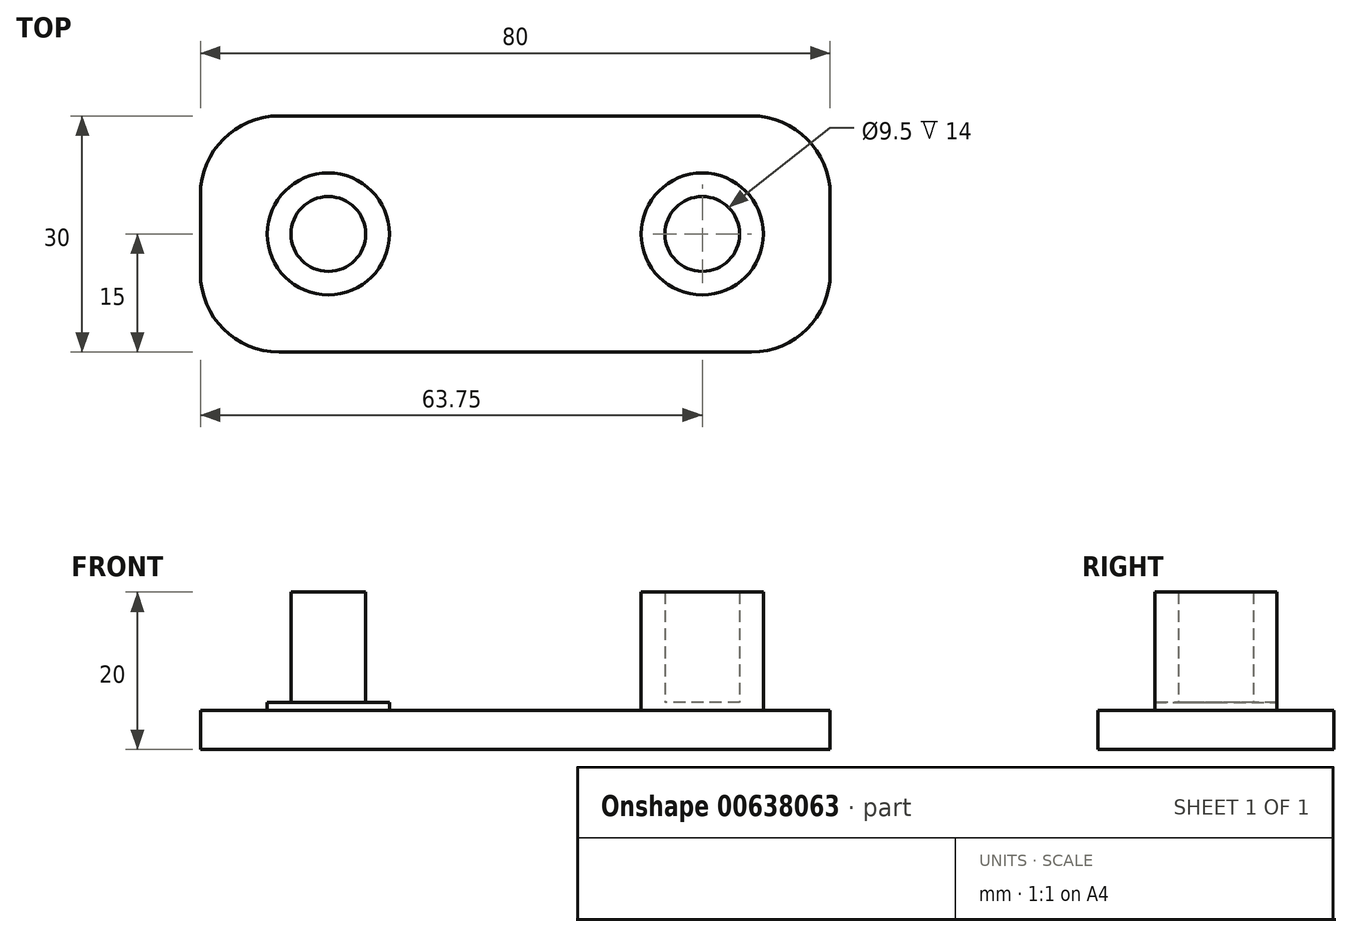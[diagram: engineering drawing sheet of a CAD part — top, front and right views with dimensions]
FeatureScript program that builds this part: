
annotation { "Feature Type Name" : "Feature", "Feature Type Description" : "" }
export const myFeature = defineFeature(function(context is Context, id is Id, definition is map)
    precondition{}
    {
        {
            var Q0;
            Q0=qCreatedBy(makeId("Top.planeOp"),FACE);
            var sketch = newSketch(context, id + "F0", { "sketchPlane" : qUnion([Q0])});
            skLineSegment(sketch, "E0.bottom", {"start": v(10, 0) * mm, "end": v(70, 0) * mm});
            skLineSegment(sketch, "E0.top", {"start": v(10, -30) * mm, "end": v(70, -30) * mm});
            skLineSegment(sketch, "E0.left", {"start": v(0, -10) * mm, "end": v(0, -20) * mm});
            skLineSegment(sketch, "E0.right", {"start": v(80, -10) * mm, "end": v(80, -20) * mm});
            skCircle(sketch, "E1", {"center": v(16.25, -15) * mm, "radius": 4.75 * mm});
            skLineSegment(sketch, "E2", {"start": v(0, -15) * mm, "end": v(80, -15) * mm, "construction": true});
            skLineSegment(sketch, "E3", {"start": v(40, 0) * mm, "end": v(40, -30) * mm, "construction": true});
            skCircle(sketch, "E4.MirrorC", {"center": v(63.75, -15) * mm, "radius": 4.75 * mm});
            skCircle(sketch, "E5", {"center": v(16.25, -15) * mm, "radius": 7.75 * mm});
            skCircle(sketch, "E6.MirrorC", {"center": v(63.75, -15) * mm, "radius": 7.75 * mm});
            skPoint(sketch, "E7.visualSharp", {"position": v(0, 0) * mm});
            skArc(sketch, "E7.filletArc", {"start": v(10, 0) * mm, "mid": v(2.93, -2.93) * mm, "end": v(0, -10) * mm});
            skPoint(sketch, "E8.visualSharp", {"position": v(80, 0) * mm});
            skArc(sketch, "E8.filletArc", {"start": v(80, -10) * mm, "mid": v(77.07, -2.93) * mm, "end": v(70, 0) * mm});
            skPoint(sketch, "E9.visualSharp", {"position": v(80, -30) * mm});
            skArc(sketch, "E9.filletArc", {"start": v(70, -30) * mm, "mid": v(77.07, -27.07) * mm, "end": v(80, -20) * mm});
            skPoint(sketch, "E10.visualSharp", {"position": v(0, -30) * mm});
            skArc(sketch, "E10.filletArc", {"start": v(0, -20) * mm, "mid": v(2.93, -27.07) * mm, "end": v(10, -30) * mm});
            skSolve(sketch);
        }
        {
            var Q0;
            Q0 = qSketchRegion(id + "F0", true);
            extrude(context, id + "F1", {"entities" : qUnion([Q0]), "depth" : 5 * mm, "offsetDistance" : 25 * mm});
        }
        {
            var Q0;
            Q0=makeQuery(id+"F0.imprint","IMPRINT",FACE,{"disambiguationData":[TD([[makeQuery(id+"F0.imprint","IMPRINT",EDGE,{"derivedFrom":sQuery(id+"F0.wireOp",EDGE,"E1")}),-1.0]])]});
            var Q1;
            Q1=makeQuery(id+"F0.imprint","IMPRINT",FACE,{"disambiguationData":[TD([[makeQuery(id+"F0.imprint","IMPRINT",EDGE,{"derivedFrom":sQuery(id+"F0.wireOp",EDGE,"E4.MirrorC")}),1.0]])]});
            extrude(context, id + "F2", {"entities" : qUnion([Q0, Q1]), "operationType" : NewBodyOperationType.ADD, "depth" : 6 * mm, "offsetDistance" : 25 * mm});
        }
        {
            var Q0;
            Q0=makeQuery(id+"F0.imprint","IMPRINT",FACE,{"disambiguationData":[TD([[makeQuery(id+"F0.imprint","IMPRINT",EDGE,{"derivedFrom":sQuery(id+"F0.wireOp",EDGE,"E1")}),1.0]])]});
            var Q1;
            Q1=makeQuery(id+"F0.imprint","IMPRINT",FACE,{"disambiguationData":[TD([[makeQuery(id+"F0.imprint","IMPRINT",EDGE,{"derivedFrom":sQuery(id+"F0.wireOp",EDGE,"E4.MirrorC")}),-1.0]])]});
            extrude(context, id + "F3", {"entities" : qUnion([Q0, Q1]), "operationType" : NewBodyOperationType.ADD, "depth" : 20 * mm, "offsetDistance" : 25 * mm});
        }
    });
